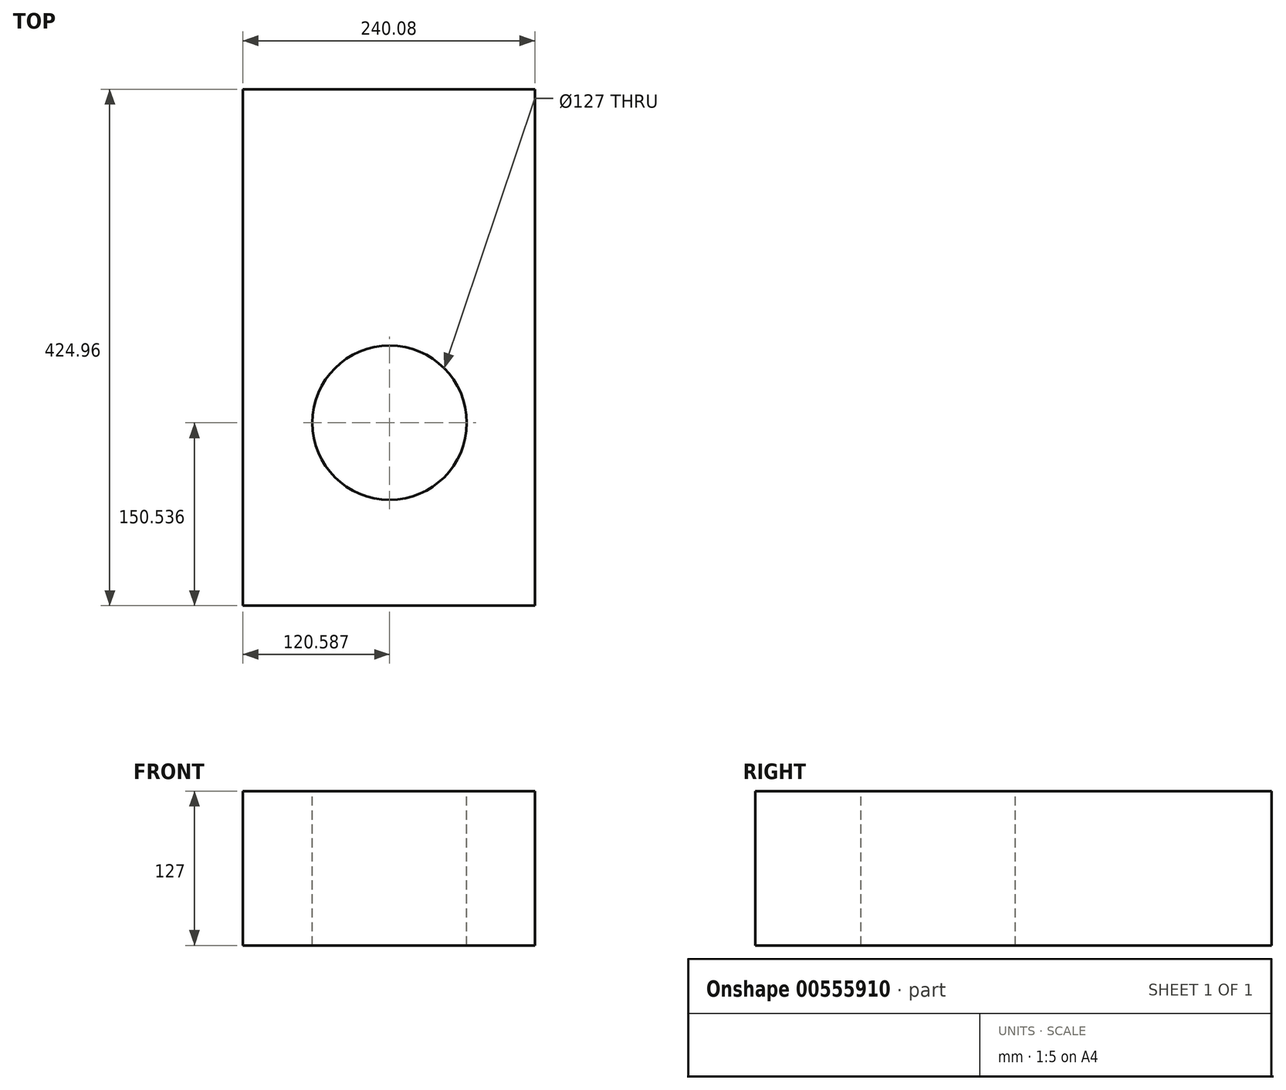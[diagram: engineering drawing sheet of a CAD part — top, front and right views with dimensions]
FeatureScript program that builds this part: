
annotation { "Feature Type Name" : "Feature", "Feature Type Description" : "" }
export const myFeature = defineFeature(function(context is Context, id is Id, definition is map)
    precondition{}
    {
        {
            var Q0;
            Q0=qCreatedBy(makeId("Top.planeOp"),FACE);
            var sketch = newSketch(context, id + "F0", { "sketchPlane" : qUnion([Q0])});
            skLineSegment(sketch, "E0.bottom", {"start": v(-120.04, 212.48) * mm, "end": v(120.04, 212.48) * mm});
            skLineSegment(sketch, "E0.top", {"start": v(-120.04, -212.48) * mm, "end": v(120.04, -212.48) * mm});
            skLineSegment(sketch, "E0.left", {"start": v(-120.04, 212.48) * mm, "end": v(-120.04, -212.48) * mm});
            skLineSegment(sketch, "E0.right", {"start": v(120.04, 212.48) * mm, "end": v(120.04, -212.48) * mm});
            skPoint(sketch, "E0.middle", {"position": v(0, 0) * mm});
            skSolve(sketch);
        }
        {
            var Q0;
            Q0=makeQuery(id+"F0.imprint","IMPRINT",FACE,{"disambiguationData":[TD([[makeQuery(id+"F0.imprint","IMPRINT",EDGE,{"derivedFrom":sQuery(id+"F0.wireOp",EDGE,"E0.bottom")}),-1.0]])]});
            extrude(context, id + "F1", {"entities" : qUnion([Q0]), "depth" : 127 * mm, "offsetDistance" : 25.4 * mm});
        }
        {
            var Q0;
            Q0=makeQuery(id+"F1.opExtrude","CAP_FACE",FACE,{"disambiguationData":[OSD([sQuery(id+"F0.wireOp",EDGE,"E0.bottom"),sQuery(id+"F0.wireOp",EDGE,"E0.top"),sQuery(id+"F0.wireOp",EDGE,"E0.left"),sQuery(id+"F0.wireOp",EDGE,"E0.right")])],"isStart":false});
            var sketch = newSketch(context, id + "F2", { "sketchPlane" : qUnion([Q0])});
            skCircle(sketch, "E1", {"center": v(0.55, -61.94) * mm, "radius": 61.95 * mm});
            skPoint(sketch, "E1.first.point", {"position": v(0, 0) * mm});
            skPoint(sketch, "E1.second.point", {"position": v(0, -123.89) * mm});
            skPoint(sketch, "E1.third.point", {"position": v(-61.24, -57.44) * mm});
            skSolve(sketch);
        }
        {
            var Q0;
            Q0=sQuery(id+"F2.wireOp",VERTEX,"E1.center");
            var Q1;
            Q1=makeQuery(id+"F1.opExtrude","SWEPT_BODY",BODY,{"disambiguationData":[OSD([sQuery(id+"F0.wireOp",EDGE,"E0.bottom"),sQuery(id+"F0.wireOp",EDGE,"E0.top"),sQuery(id+"F0.wireOp",EDGE,"E0.left"),sQuery(id+"F0.wireOp",EDGE,"E0.right")])]});
            hole(context, id + "F3", {"style" : HoleStyle.SIMPLE, "endStyle" : HoleEndStyle.THROUGH, "holeDiameter" : 127 * mm, "isTappedThrough" : true, "tappedDepth" : 12.7 * mm, "tapClearance" : 3, "locations" : qUnion([Q0]), "scope" : qUnion([Q1])});
        }
    });
